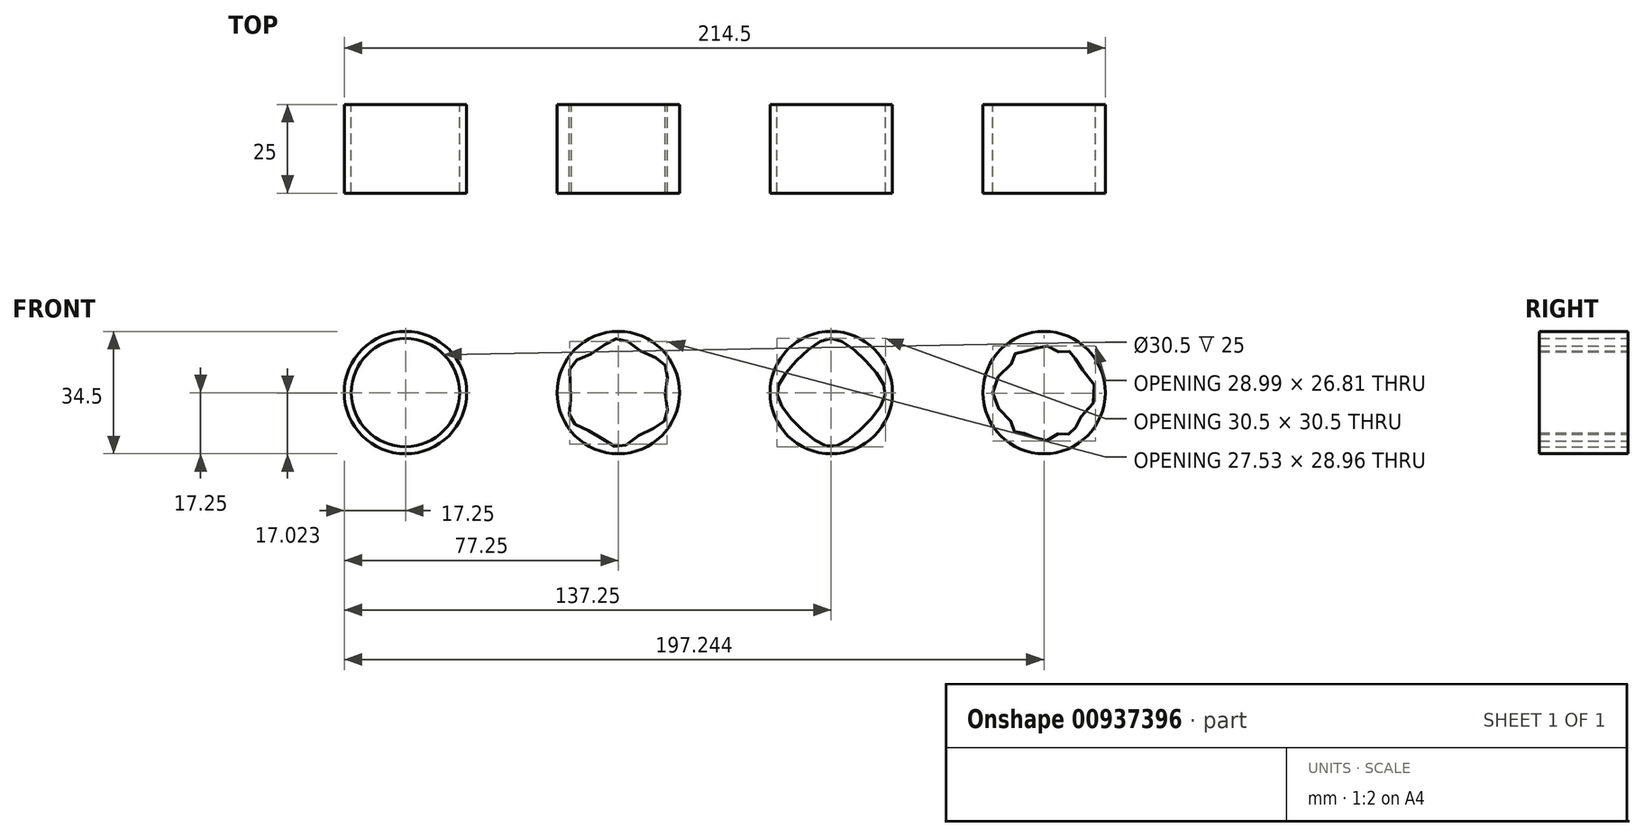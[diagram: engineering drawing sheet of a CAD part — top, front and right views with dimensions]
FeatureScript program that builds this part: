
annotation { "Feature Type Name" : "Feature", "Feature Type Description" : "" }
export const myFeature = defineFeature(function(context is Context, id is Id, definition is map)
    precondition{}
    {
        {
            var Q0;
            Q0=qCreatedBy(makeId("Front.planeOp"),FACE);
            var sketch = newSketch(context, id + "F0", { "sketchPlane" : qUnion([Q0])});
            skCircle(sketch, "E0", {"center": v(0, 0) * mm, "radius": 17.25 * mm});
            skCircle(sketch, "E1", {"center": v(0, 0) * mm, "radius": 15.25 * mm, "construction": true});
            skCircle(sketch, "E2", {"center": v(60, 0) * mm, "radius": 17.25 * mm});
            skCircle(sketch, "E3", {"center": v(60, 0) * mm, "radius": 15.25 * mm, "construction": true});
            skCircle(sketch, "E4", {"center": v(60, 8.93) * mm, "radius": 6.32 * mm, "construction": true});
            skCircle(sketch, "E5", {"center": v(51.07, 0) * mm, "radius": 6.32 * mm, "construction": true});
            skCircle(sketch, "E6", {"center": v(68.93, 0) * mm, "radius": 6.32 * mm, "construction": true});
            skCircle(sketch, "E7", {"center": v(60, -8.93) * mm, "radius": 6.32 * mm, "construction": true});
            skLineSegment(sketch, "E8", {"start": v(60, 19.16) * mm, "end": v(60, -32.04) * mm, "construction": true});
            skLineSegment(sketch, "E9", {"start": v(45.8, 0) * mm, "end": v(103.75, 0) * mm, "construction": true});
            skPoint(sketch, "E10", {"position": v(75.25, 0) * mm});
            skPoint(sketch, "E11", {"position": v(44.75, 0) * mm});
            skPoint(sketch, "E12", {"position": v(60, -15.25) * mm});
            skPoint(sketch, "E13", {"position": v(60, 15.25) * mm});
            skFitSpline(sketch, "E14", {"points": [v(60, 15.25) * mm, v(56.23, 14) * mm, v(50.63, 9.37) * mm, v(46, 3.77) * mm, v(44.75, 0) * mm, v(46, -3.77) * mm, v(50.63, -9.37) * mm, v(56.23, -14) * mm, v(60, -15.25) * mm, v(63.77, -14) * mm, v(69.37, -9.37) * mm, v(74, -3.77) * mm, v(75.25, 0) * mm, v(74, 3.77) * mm, v(69.37, 9.37) * mm, v(63.77, 14) * mm, v(60, 15.25) * mm]});
            skLineSegment(sketch, "E15", {"start": v(40.74, 19.26) * mm, "end": v(81.53, -21.53) * mm, "construction": true});
            skLineSegment(sketch, "E16", {"start": v(44.83, -15.17) * mm, "end": v(83.24, 23.24) * mm, "construction": true});
            skPoint(sketch, "E17", {"position": v(47.8, 12.2) * mm});
            skCircle(sketch, "E18", {"center": v(60, 0) * mm, "radius": 13.25 * mm, "construction": true});
            skCircle(sketch, "E19", {"center": v(60, 0) * mm, "radius": 14.5 * mm, "construction": true});
            skCircle(sketch, "E20", {"center": v(0, 10.17) * mm, "radius": 5.08 * mm, "construction": true});
            skCircle(sketch, "E21", {"center": v(8.8, 5.08) * mm, "radius": 5.08 * mm, "construction": true});
            skCircle(sketch, "E22", {"center": v(8.8, -5.08) * mm, "radius": 5.08 * mm, "construction": true});
            skCircle(sketch, "E23", {"center": v(0, -10.17) * mm, "radius": 5.08 * mm, "construction": true});
            skCircle(sketch, "E24", {"center": v(-8.8, -5.08) * mm, "radius": 5.08 * mm, "construction": true});
            skCircle(sketch, "E25", {"center": v(-8.8, 5.08) * mm, "radius": 5.08 * mm, "construction": true});
            skFitSpline(sketch, "E26", {"points": [v(2.7, 14.48) * mm, v(0, 15.25) * mm, v(-2.7, 14.48) * mm, v(-6.62, 11.47) * mm, v(-11.2, 9.57) * mm, v(-13.2, 7.62) * mm, v(-13.88, 4.9) * mm, v(-13.25, 0) * mm, v(-13.88, -4.9) * mm, v(-13.2, -7.62) * mm, v(-11.2, -9.57) * mm, v(-6.63, -11.47) * mm, v(-2.7, -14.48) * mm, v(0, -15.25) * mm, v(2.7, -14.48) * mm, v(6.62, -11.47) * mm, v(11.2, -9.57) * mm, v(13.2, -7.63) * mm, v(13.88, -4.9) * mm, v(13.25, 0) * mm, v(13.88, 4.9) * mm, v(13.2, 7.62) * mm, v(11.2, 9.57) * mm, v(6.63, 11.47) * mm, v(2.7, 14.48) * mm]});
            skPoint(sketch, "E27", {"position": v(-13.2, 7.63) * mm});
            skPoint(sketch, "E28", {"position": v(13.2, 7.63) * mm});
            skLineSegment(sketch, "E29", {"start": v(-10.57, 18.32) * mm, "end": v(13.2, -22.85) * mm, "construction": true});
            skLineSegment(sketch, "E30", {"start": v(-12.78, -22.14) * mm, "end": v(12.55, 21.73) * mm, "construction": true});
            skPoint(sketch, "E31", {"position": v(4.4, 7.62) * mm});
            skPoint(sketch, "E32", {"position": v(8.8, 0) * mm});
            skPoint(sketch, "E33", {"position": v(4.4, -7.62) * mm});
            skPoint(sketch, "E34", {"position": v(-4.4, -7.63) * mm});
            skPoint(sketch, "E35", {"position": v(-8.8, 0) * mm});
            skPoint(sketch, "E36", {"position": v(-4.4, 7.63) * mm});
            skCircle(sketch, "E37", {"center": v(0, 0) * mm, "radius": 13.25 * mm, "construction": true});
            skCircle(sketch, "E38", {"center": v(0, 0) * mm, "radius": 14.73 * mm, "construction": true});
            skCircle(sketch, "E39", {"center": v(-60, 0) * mm, "radius": 17.25 * mm});
            skCircle(sketch, "E40", {"center": v(-60, 0) * mm, "radius": 15.25 * mm});
            skCircle(sketch, "E41", {"center": v(112.75, 0) * mm, "radius": 7.25 * mm, "construction": true});
            skCircle(sketch, "E42", {"center": v(127.25, 0) * mm, "radius": 7.25 * mm, "construction": true});
            skCircle(sketch, "E43", {"center": v(113.52, 9.47) * mm, "radius": 2.25 * mm, "construction": true});
            skCircle(sketch, "E44", {"center": v(126.48, 9.47) * mm, "radius": 2.25 * mm, "construction": true});
            skCircle(sketch, "E45", {"center": v(113.3, -9.48) * mm, "radius": 2.25 * mm, "construction": true});
            skCircle(sketch, "E46", {"center": v(126.7, -9.48) * mm, "radius": 2.25 * mm, "construction": true});
            skCircle(sketch, "E47", {"center": v(120, -9.18) * mm, "radius": 4.45 * mm, "construction": true});
            skCircle(sketch, "E48", {"center": v(120, 8.93) * mm, "radius": 4.25 * mm, "construction": true});
            skLineSegment(sketch, "E49", {"start": v(96.93, 0) * mm, "end": v(191.3, 0) * mm, "construction": true});
            skLineSegment(sketch, "E50", {"start": v(120, 37.15) * mm, "end": v(120, -26.48) * mm, "construction": true});
            skPoint(sketch, "E51", {"position": v(120, 0) * mm});
            skCircle(sketch, "E52", {"center": v(120, 0) * mm, "radius": 17.25 * mm});
            skFitSpline(sketch, "E53", {"points": [v(105.5, 0) * mm, v(107, -4.42) * mm, v(110.6, -7.86) * mm, v(111.1, -9.9) * mm, v(112, -11.32) * mm, v(113.66, -11.7) * mm, v(115.45, -11.37) * mm, v(117.37, -12.77) * mm, v(120, -13.63) * mm, v(122.63, -12.77) * mm, v(124.55, -11.37) * mm, v(126.35, -11.7) * mm, v(128, -11.32) * mm, v(128.9, -9.9) * mm, v(129.4, -7.86) * mm, v(132.41, -5.09) * mm, v(134.5, 0) * mm, v(132.44, 5.07) * mm, v(129.32, 7.95) * mm, v(128.6, 10.24) * mm, v(127.75, 11.33) * mm, v(126.43, 11.72) * mm, v(124.28, 11.48) * mm, v(122.02, 12.67) * mm, v(120, 13.18) * mm, v(117.98, 12.67) * mm, v(115.72, 11.48) * mm, v(113.68, 11.71) * mm, v(112.25, 11.33) * mm, v(111.37, 10.13) * mm, v(110.68, 7.95) * mm, v(106.98, 4.39) * mm, v(105.5, 0) * mm]});
            skLineSegment(sketch, "E54", {"start": v(120, 0) * mm, "end": v(141.2, -30.03) * mm, "construction": true});
            skLineSegment(sketch, "E55", {"start": v(120, 0) * mm, "end": v(132.63, 18.46) * mm, "construction": true});
            skLineSegment(sketch, "E56", {"start": v(120, 0) * mm, "end": v(107.18, 18.73) * mm, "construction": true});
            skLineSegment(sketch, "E57", {"start": v(120, 0) * mm, "end": v(104.34, -22.19) * mm, "construction": true});
            skCircle(sketch, "E58", {"center": v(120, 0) * mm, "radius": 12.25 * mm, "construction": true});
            skCircle(sketch, "E59", {"center": v(110.68, 7.95) * mm, "radius": 0.97 * mm, "construction": true});
            skCircle(sketch, "E60", {"center": v(110.6, -7.86) * mm, "radius": 0.9 * mm, "construction": true});
            skCircle(sketch, "E61", {"center": v(115.45, -11.37) * mm, "radius": 0.6 * mm, "construction": true});
            skCircle(sketch, "E62", {"center": v(124.55, -11.37) * mm, "radius": 0.6 * mm, "construction": true});
            skCircle(sketch, "E63", {"center": v(129.4, -7.86) * mm, "radius": 0.9 * mm, "construction": true});
            skCircle(sketch, "E64", {"center": v(129.32, 7.95) * mm, "radius": 0.97 * mm, "construction": true});
            skCircle(sketch, "E65", {"center": v(124.28, 11.48) * mm, "radius": 0.73 * mm, "construction": true});
            skCircle(sketch, "E66", {"center": v(115.72, 11.48) * mm, "radius": 0.73 * mm, "construction": true});
            skLineSegment(sketch, "E67", {"start": v(111.37, 10.13) * mm, "end": v(113.68, 11.71) * mm, "construction": true});
            skLineSegment(sketch, "E68", {"start": v(117.98, 12.67) * mm, "end": v(122.02, 12.67) * mm, "construction": true});
            skLineSegment(sketch, "E69", {"start": v(126.43, 11.72) * mm, "end": v(128.6, 10.24) * mm, "construction": true});
            skLineSegment(sketch, "E70", {"start": v(117.37, -12.77) * mm, "end": v(122.63, -12.77) * mm, "construction": true});
            skLineSegment(sketch, "E71", {"start": v(126.35, -11.7) * mm, "end": v(128.9, -9.9) * mm, "construction": true});
            skLineSegment(sketch, "E72", {"start": v(111.1, -9.9) * mm, "end": v(113.66, -11.7) * mm, "construction": true});
            skSolve(sketch);
        }
        {
            var Q0;
            Q0=makeQuery(id+"F0.imprint","IMPRINT",FACE,{"disambiguationData":[TD([[makeQuery(id+"F0.imprint","IMPRINT",EDGE,{"derivedFrom":sQuery(id+"F0.wireOp",EDGE,"E2")}),1.0]])]});
            var Q1;
            Q1=makeQuery(id+"F0.imprint","IMPRINT",FACE,{"disambiguationData":[TD([[makeQuery(id+"F0.imprint","IMPRINT",EDGE,{"derivedFrom":sQuery(id+"F0.wireOp",EDGE,"E0")}),1.0]])]});
            var Q2;
            Q2=makeQuery(id+"F0.imprint","IMPRINT",FACE,{"disambiguationData":[TD([[makeQuery(id+"F0.imprint","IMPRINT",EDGE,{"derivedFrom":sQuery(id+"F0.wireOp",EDGE,"E39")}),1.0]])]});
            var Q3;
            Q3=makeQuery(id+"F0.imprint","IMPRINT",FACE,{"disambiguationData":[TD([[makeQuery(id+"F0.imprint","IMPRINT",EDGE,{"derivedFrom":sQuery(id+"F0.wireOp",EDGE,"E52")}),1.0]])]});
            extrude(context, id + "F1", {"entities" : qUnion([Q0, Q1, Q2, Q3]), "depth" : 25 * mm, "offsetDistance" : 25 * mm});
        }
    });
